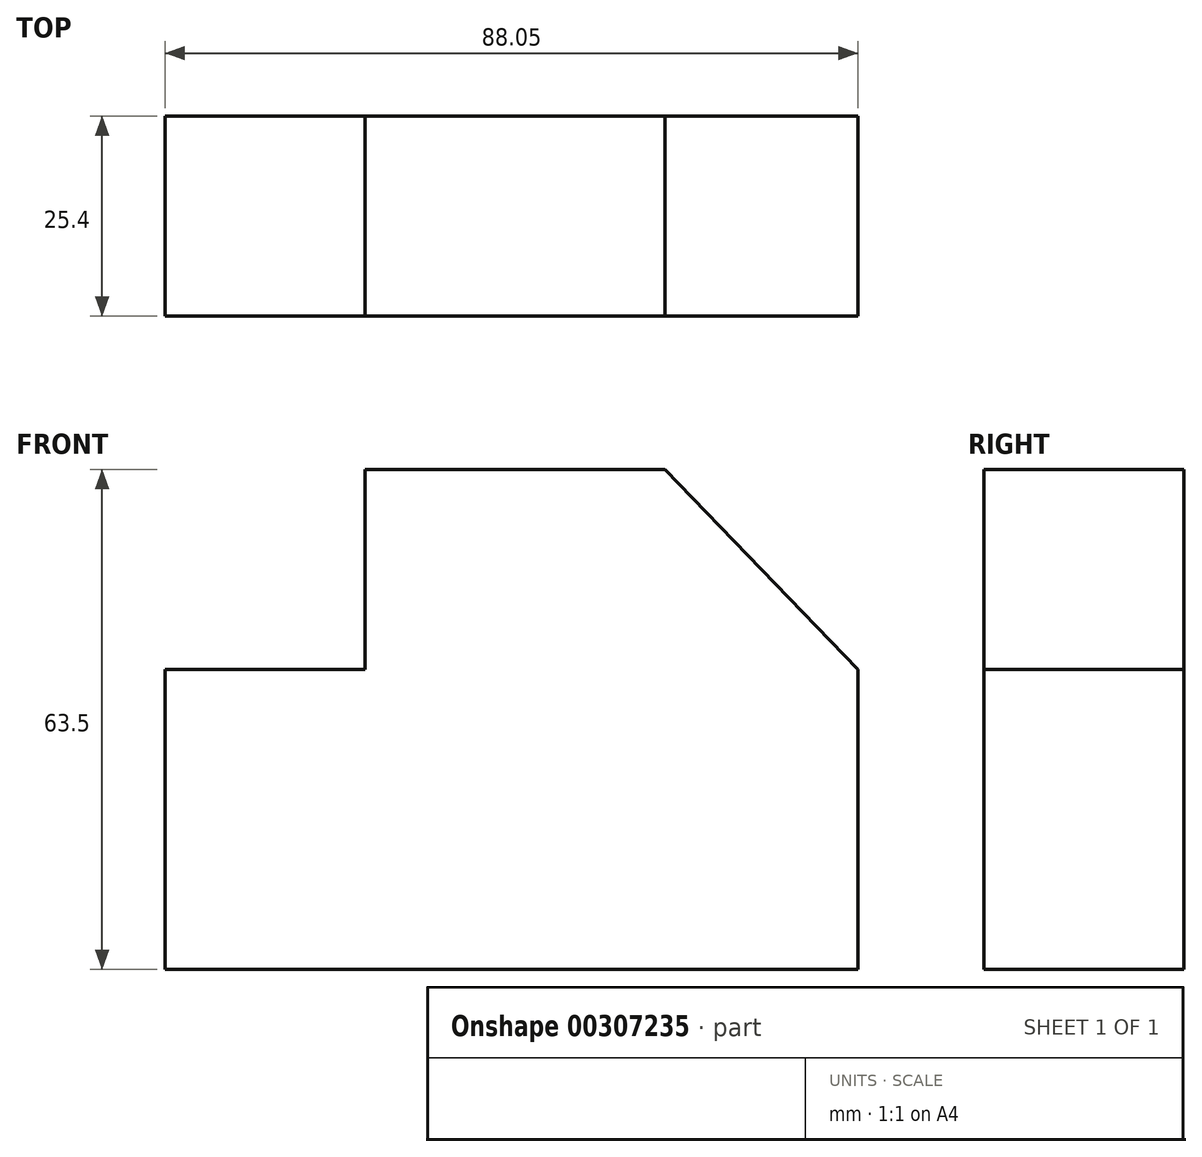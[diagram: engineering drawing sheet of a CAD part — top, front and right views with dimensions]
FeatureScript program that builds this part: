
annotation { "Feature Type Name" : "Feature", "Feature Type Description" : "" }
export const myFeature = defineFeature(function(context is Context, id is Id, definition is map)
    precondition{}
    {
        {
            var Q0;
            Q0=qCreatedBy(makeId("Front.planeOp"),FACE);
            var sketch = newSketch(context, id + "F0", { "sketchPlane" : qUnion([Q0])});
            skLineSegment(sketch, "E0", {"start": v(11.49, 45.73) * mm, "end": v(-26.61, 45.73) * mm});
            skLineSegment(sketch, "E1", {"start": v(-26.61, 45.73) * mm, "end": v(-26.61, 20.33) * mm});
            skLineSegment(sketch, "E2", {"start": v(-26.61, 20.33) * mm, "end": v(-52.01, 20.33) * mm});
            skLineSegment(sketch, "E3", {"start": v(-52.01, 20.33) * mm, "end": v(-52.01, -17.77) * mm});
            skLineSegment(sketch, "E4", {"start": v(-52.01, -17.77) * mm, "end": v(36.04, -17.77) * mm});
            skLineSegment(sketch, "E5", {"start": v(36.04, -17.77) * mm, "end": v(36.04, 20.33) * mm});
            skLineSegment(sketch, "E6", {"start": v(36.04, 20.33) * mm, "end": v(11.49, 45.73) * mm});
            skSolve(sketch);
        }
        {
            var Q0;
            Q0 = qSketchRegion(id + "F0", true);
            extrude(context, id + "F1", {"entities" : qUnion([Q0]), "depth" : 25.4 * mm});
        }
    });
